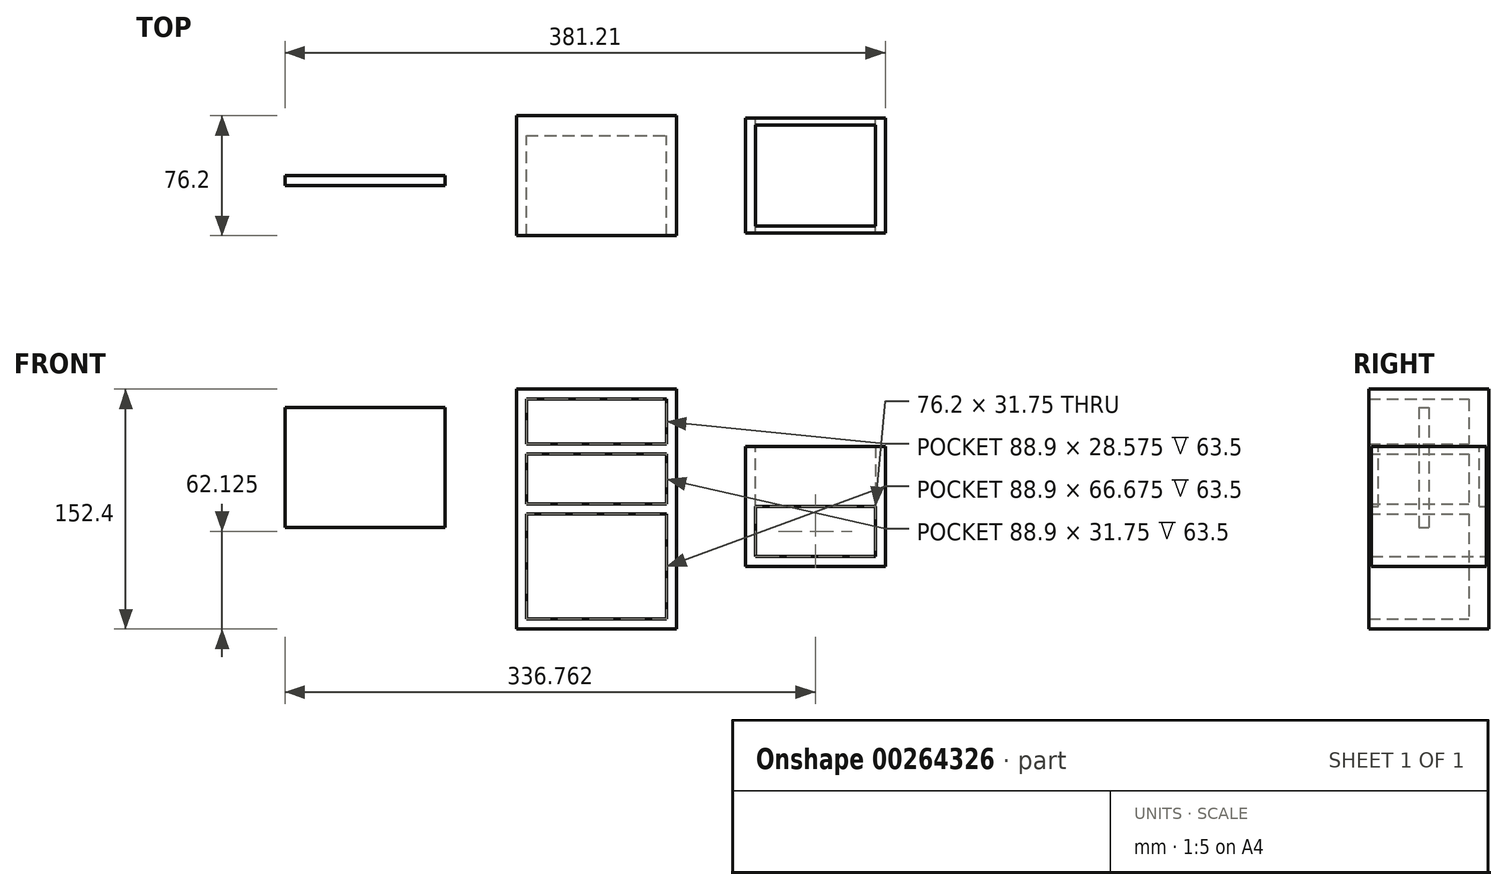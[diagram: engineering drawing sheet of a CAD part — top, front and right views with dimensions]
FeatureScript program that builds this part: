
annotation { "Feature Type Name" : "Feature", "Feature Type Description" : "" }
export const myFeature = defineFeature(function(context is Context, id is Id, definition is map)
    precondition{}
    {
        {
            var Q0;
            Q0=qCreatedBy(makeId("Top.planeOp"),FACE);
            var sketch = newSketch(context, id + "F0", { "sketchPlane" : qUnion([Q0])});
            skLineSegment(sketch, "E0.bottom", {"start": v(-50.8, 38.1) * mm, "end": v(50.8, 38.1) * mm});
            skLineSegment(sketch, "E0.top", {"start": v(-50.8, -38.1) * mm, "end": v(50.8, -38.1) * mm});
            skLineSegment(sketch, "E0.left", {"start": v(-50.8, 38.1) * mm, "end": v(-50.8, -38.1) * mm});
            skLineSegment(sketch, "E0.right", {"start": v(50.8, 38.1) * mm, "end": v(50.8, -38.1) * mm});
            skPoint(sketch, "E0.middle", {"position": v(0, 0) * mm});
            skSolve(sketch);
        }
        {
            var Q0;
            Q0=makeQuery(id+"F0.imprint","IMPRINT",FACE,{"disambiguationData":[TD([[makeQuery(id+"F0.imprint","IMPRINT",EDGE,{"derivedFrom":sQuery(id+"F0.wireOp",EDGE,"E0.bottom")}),-1.0]])]});
            extrude(context, id + "F1", {"entities" : qUnion([Q0]), "endBound" : BoundingType.SYMMETRIC, "depth" : 152.4 * mm});
        }
        {
            var Q0;
            Q0=qCreatedBy(makeId("Front.planeOp"),FACE);
            var sketch = newSketch(context, id + "F2", { "sketchPlane" : qUnion([Q0])});
            skLineSegment(sketch, "E1", {"start": v(0, 0) * mm, "end": v(0, 38.1) * mm});
            skLineSegment(sketch, "E2", {"start": v(0, 0) * mm, "end": v(0, 19.05) * mm});
            skLineSegment(sketch, "E3.bottom", {"start": v(-44.45, 69.85) * mm, "end": v(44.45, 69.85) * mm});
            skLineSegment(sketch, "E3.top", {"start": v(-44.45, -31.75) * mm, "end": v(44.45, -31.75) * mm});
            skLineSegment(sketch, "E3.left", {"start": v(-44.45, 69.85) * mm, "end": v(-44.45, -31.75) * mm});
            skLineSegment(sketch, "E3.right", {"start": v(44.45, 69.85) * mm, "end": v(44.45, -31.75) * mm});
            skPoint(sketch, "E3.middle", {"position": v(0, 19.05) * mm});
            skLineSegment(sketch, "E4", {"start": v(0, -31.75) * mm, "end": v(0, -57.15) * mm});
            skPoint(sketch, "E4.endSnap0", {"position": v(0, -31.75) * mm});
            skLineSegment(sketch, "E5.bottom", {"start": v(-44.45, -44.45) * mm, "end": v(44.45, -44.45) * mm});
            skLineSegment(sketch, "E5.top", {"start": v(-44.45, -69.85) * mm, "end": v(44.45, -69.85) * mm});
            skLineSegment(sketch, "E5.left", {"start": v(-44.45, -44.45) * mm, "end": v(-44.45, -69.85) * mm});
            skLineSegment(sketch, "E5.right", {"start": v(44.45, -44.45) * mm, "end": v(44.45, -69.85) * mm});
            skPoint(sketch, "E5.middle", {"position": v(0, -57.15) * mm});
            skLineSegment(sketch, "E6.bottom", {"start": v(-44.45, 41.28) * mm, "end": v(44.45, 41.28) * mm});
            skLineSegment(sketch, "E6.top", {"start": v(-44.45, 34.92) * mm, "end": v(44.45, 34.92) * mm});
            skLineSegment(sketch, "E6.left", {"start": v(-44.45, 41.28) * mm, "end": v(-44.45, 34.92) * mm});
            skLineSegment(sketch, "E6.right", {"start": v(44.45, 41.28) * mm, "end": v(44.45, 34.92) * mm});
            skPoint(sketch, "E6.middle", {"position": v(0, 38.1) * mm});
            skLineSegment(sketch, "E7.bottom", {"start": v(-44.45, 3.18) * mm, "end": v(44.45, 3.18) * mm});
            skLineSegment(sketch, "E7.top", {"start": v(-44.45, -3.17) * mm, "end": v(44.45, -3.17) * mm});
            skLineSegment(sketch, "E7.left", {"start": v(-44.45, 3.18) * mm, "end": v(-44.45, -3.17) * mm});
            skLineSegment(sketch, "E7.right", {"start": v(44.45, 3.18) * mm, "end": v(44.45, -3.17) * mm});
            skPoint(sketch, "E7.middle", {"position": v(0, 0) * mm});
            skLineSegment(sketch, "E8", {"start": v(-44.45, -44.45) * mm, "end": v(-44.45, -38.1) * mm});
            skLineSegment(sketch, "E9", {"start": v(-44.45, -38.1) * mm, "end": v(44.45, -38.1) * mm});
            skLineSegment(sketch, "E10", {"start": v(44.45, -38.1) * mm, "end": v(44.45, -44.45) * mm});
            skLineSegment(sketch, "E11.bottom", {"start": v(-197.75, 64.7) * mm, "end": v(-96.15, 64.7) * mm});
            skLineSegment(sketch, "E11.top", {"start": v(-197.75, -11.5) * mm, "end": v(-96.15, -11.5) * mm});
            skLineSegment(sketch, "E11.left", {"start": v(-197.75, 64.7) * mm, "end": v(-197.75, -11.5) * mm});
            skLineSegment(sketch, "E11.right", {"start": v(-96.15, 64.7) * mm, "end": v(-96.15, -11.5) * mm});
            skPoint(sketch, "E11.middle", {"position": v(-146.95, 26.6) * mm});
            skLineSegment(sketch, "E12", {"start": v(-44.45, -31.75) * mm, "end": v(-44.45, -38.1) * mm});
            skLineSegment(sketch, "E13", {"start": v(44.45, -31.75) * mm, "end": v(44.45, -38.1) * mm});
            skPoint(sketch, "E14.middle", {"position": v(139.01, 1.8) * mm});
            skLineSegment(sketch, "E15.bottom", {"start": v(94.56, -36.3) * mm, "end": v(183.46, -36.3) * mm});
            skLineSegment(sketch, "E15.left", {"start": v(94.56, -36.3) * mm, "end": v(94.56, 39.9) * mm});
            skLineSegment(sketch, "E15.right", {"start": v(183.46, -36.3) * mm, "end": v(183.46, 39.9) * mm});
            skLineSegment(sketch, "E16", {"start": v(94.56, -29.95) * mm, "end": v(183.46, -29.95) * mm});
            skLineSegment(sketch, "E17", {"start": v(139.01, 1.8) * mm, "end": v(139.01, 39.9) * mm});
            skLineSegment(sketch, "E18", {"start": v(139.01, 39.9) * mm, "end": v(94.56, 39.9) * mm});
            skLineSegment(sketch, "E19", {"start": v(139.01, 39.9) * mm, "end": v(183.46, 39.9) * mm});
            skLineSegment(sketch, "E20", {"start": v(139.01, 1.8) * mm, "end": v(100.91, 1.8) * mm});
            skLineSegment(sketch, "E21", {"start": v(100.91, 1.8) * mm, "end": v(139.01, 1.8) * mm});
            skLineSegment(sketch, "E22", {"start": v(177.11, 1.8) * mm, "end": v(139.01, 1.8) * mm});
            skLineSegment(sketch, "E23", {"start": v(100.91, 1.8) * mm, "end": v(100.91, -36.3) * mm});
            skLineSegment(sketch, "E24", {"start": v(100.91, -36.3) * mm, "end": v(100.91, 39.9) * mm});
            skLineSegment(sketch, "E25", {"start": v(100.91, 39.9) * mm, "end": v(177.11, 39.9) * mm});
            skLineSegment(sketch, "E26", {"start": v(177.11, 39.9) * mm, "end": v(177.11, 1.8) * mm});
            skLineSegment(sketch, "E27", {"start": v(177.11, -29.95) * mm, "end": v(177.11, 1.8) * mm});
            skLineSegment(sketch, "E28", {"start": v(139.01, 39.9) * mm, "end": v(139.01, 33.55) * mm});
            skLineSegment(sketch, "E29", {"start": v(139.01, 33.55) * mm, "end": v(183.46, 33.55) * mm});
            skLineSegment(sketch, "E30", {"start": v(183.46, 33.55) * mm, "end": v(94.56, 33.55) * mm});
            skSolve(sketch);
        }
        {
            var Q0;
            Q0=makeQuery(id+"F2.imprint","IMPRINT",FACE,{"disambiguationData":[TD([[makeQuery(id+"F2.imprint","IMPRINT",EDGE,{"derivedFrom":sQuery(id+"F2.wireOp",EDGE,"E3.bottom")}),-1.0]])]});
            var Q1;
            Q1=makeQuery(id+"F2.imprint","IMPRINT",FACE,{"disambiguationData":[TD([[makeQuery(id+"F2.imprint","IMPRINT",EDGE,{"derivedFrom":sQuery(id+"F2.wireOp",EDGE,"E5.top")}),1.0]])]});
            var Q2;
            {var subQ5=sQuery(id+"F2.wireOp",EDGE,"E2");var subQ6=sQuery(id+"F2.wireOp",EDGE,"E1");var subQ7=makeQuery(id+"F2.imprint","INTERSECT",VERTEX,{"derivedFrom":[subQ6,subQ5]});Q2=makeQuery(id+"F2.imprint","IMPRINT",FACE,{"disambiguationData":[TD([[makeQuery(id+"F2.imprint","IMPRINT",EDGE,{"disambiguationData":[TD([[subQ7,-1.0]])],"derivedFrom":subQ6}),1.0]])]});}
            var Q3;
            {var subQ5=sQuery(id+"F2.wireOp",EDGE,"E2");var subQ7=sQuery(id+"F2.wireOp",EDGE,"E1");var subQ9=makeQuery(id+"F2.imprint","INTERSECT",VERTEX,{"derivedFrom":[subQ7,subQ5]});Q3=makeQuery(id+"F2.imprint","IMPRINT",FACE,{"disambiguationData":[TD([[makeQuery(id+"F2.imprint","IMPRINT",EDGE,{"disambiguationData":[TD([[subQ9,-1.0]])],"derivedFrom":subQ7}),-1.0]])]});}
            var Q4;
            {var subQ3=sQuery(id+"F2.wireOp",EDGE,"E7.top");Q4=makeQuery(id+"F2.imprint","IMPRINT",FACE,{"disambiguationData":[TD([[makeQuery(id+"F2.imprint","IMPRINT",EDGE,{"derivedFrom":subQ3}),-1.0]])]});}
            var Q5;
            {var subQ5=sQuery(id+"F2.wireOp",EDGE,"E10");Q5=makeQuery(id+"F2.imprint","IMPRINT",FACE,{"disambiguationData":[TD([[makeQuery(id+"F2.imprint","IMPRINT",EDGE,{"derivedFrom":subQ5}),-1.0]])]});}
            var Q6;
            {var subQ5=sQuery(id+"F2.wireOp",EDGE,"E8");Q6=makeQuery(id+"F2.imprint","IMPRINT",FACE,{"disambiguationData":[TD([[makeQuery(id+"F2.imprint","IMPRINT",EDGE,{"derivedFrom":subQ5}),-1.0]])]});}
            var Q7;
            {var subQ0=sQuery(id+"F2.wireOp",EDGE,"E12");Q7=makeQuery(id+"F2.imprint","IMPRINT",FACE,{"disambiguationData":[TD([[makeQuery(id+"F2.imprint","IMPRINT",EDGE,{"derivedFrom":subQ0}),1.0]])]});}
            var Q8;
            {var subQ0=sQuery(id+"F2.wireOp",EDGE,"E13");Q8=makeQuery(id+"F2.imprint","IMPRINT",FACE,{"disambiguationData":[TD([[makeQuery(id+"F2.imprint","IMPRINT",EDGE,{"derivedFrom":subQ0}),-1.0]])]});}
            extrude(context, id + "F3", {"entities" : qUnion([Q0, Q1, Q2, Q3, Q4, Q5, Q6, Q7, Q8]), "operationType" : NewBodyOperationType.REMOVE, "depth" : 50.8 * mm});
        }
        {
            var Q0;
            Q0=makeQuery(id+"F3.boolean.opBoolean","COPY",FACE,{"derivedFrom":makeQuery(id+"F3.opExtrude","CAP_FACE",FACE,{"disambiguationData":[OSD([sQuery(id+"F2.wireOp",EDGE,"E3.bottom"),sQuery(id+"F2.wireOp",EDGE,"E3.top"),sQuery(id+"F2.wireOp",EDGE,"E3.left"),sQuery(id+"F2.wireOp",EDGE,"E3.right")])],"isStart":true})});
            var Q1;
            Q1=makeQuery(id+"F3.boolean.opBoolean","COPY",FACE,{"derivedFrom":makeQuery(id+"F3.opExtrude","CAP_FACE",FACE,{"disambiguationData":[OSD([sQuery(id+"F2.wireOp",EDGE,"E3.left"),sQuery(id+"F2.wireOp",EDGE,"E3.right"),sQuery(id+"F2.wireOp",EDGE,"E6.top"),sQuery(id+"F2.wireOp",EDGE,"E7.bottom")])],"isStart":true})});
            var Q2;
            Q2=makeQuery(id+"F3.boolean.opBoolean","COPY",FACE,{"derivedFrom":makeQuery(id+"F3.opExtrude","CAP_FACE",FACE,{"disambiguationData":[OSD([sQuery(id+"F2.wireOp",EDGE,"E3.left"),sQuery(id+"F2.wireOp",EDGE,"E3.right"),sQuery(id+"F2.wireOp",EDGE,"E5.top"),sQuery(id+"F2.wireOp",EDGE,"E5.left"),sQuery(id+"F2.wireOp",EDGE,"E5.right"),sQuery(id+"F2.wireOp",EDGE,"E7.top"),sQuery(id+"F2.wireOp",EDGE,"E8"),sQuery(id+"F2.wireOp",EDGE,"E10"),sQuery(id+"F2.wireOp",EDGE,"E12"),sQuery(id+"F2.wireOp",EDGE,"E13")])],"isStart":true})});
            extrude(context, id + "F4", {"entities" : qUnion([Q0, Q1, Q2]), "operationType" : NewBodyOperationType.REMOVE, "oppositeDirection" : true, "depth" : 25.4 * mm});
        }
        {
            var Q0;
            Q0=makeQuery(id+"F2.imprint","IMPRINT",FACE,{"disambiguationData":[TD([[makeQuery(id+"F2.imprint","IMPRINT",EDGE,{"derivedFrom":sQuery(id+"F2.wireOp",EDGE,"E11.bottom")}),-1.0]])]});
            extrude(context, id + "F5", {"entities" : qUnion([Q0]), "depth" : 6.35 * mm});
        }
        {
            var Q0;
            {var subQ2=sQuery(id+"F2.wireOp",EDGE,"E16");var subQ4=sQuery(id+"F2.wireOp",EDGE,"E15.left");var subQ5=makeQuery(id+"F2.imprint","INTERSECT",VERTEX,{"derivedFrom":[subQ4,subQ2]});Q0=makeQuery(id+"F2.imprint","IMPRINT",FACE,{"disambiguationData":[TD([[makeQuery(id+"F2.imprint","IMPRINT",EDGE,{"disambiguationData":[TD([[subQ5,-1.0]])],"derivedFrom":subQ4}),-1.0]])]});}
            var Q1;
            {var subQ0=sQuery(id+"F2.wireOp",EDGE,"E17");Q1=makeQuery(id+"F2.imprint","IMPRINT",FACE,{"disambiguationData":[TD([[makeQuery(id+"F2.imprint","IMPRINT",EDGE,{"derivedFrom":subQ0}),1.0]])]});}
            var Q2;
            {var subQ0=sQuery(id+"F2.wireOp",EDGE,"E17");Q2=makeQuery(id+"F2.imprint","IMPRINT",FACE,{"disambiguationData":[TD([[makeQuery(id+"F2.imprint","IMPRINT",EDGE,{"derivedFrom":subQ0}),-1.0]])]});}
            var Q3;
            {var subQ1=sQuery(id+"F2.wireOp",EDGE,"E21");Q3=makeQuery(id+"F2.imprint","IMPRINT",FACE,{"disambiguationData":[TD([[makeQuery(id+"F2.imprint","IMPRINT",EDGE,{"derivedFrom":subQ1}),-1.0]])]});}
            var Q4;
            {var subQ0=sQuery(id+"F2.wireOp",EDGE,"E27");Q4=makeQuery(id+"F2.imprint","IMPRINT",FACE,{"disambiguationData":[TD([[makeQuery(id+"F2.imprint","IMPRINT",EDGE,{"derivedFrom":subQ0}),-1.0]])]});}
            var Q5;
            {var subQ0=sQuery(id+"F2.wireOp",EDGE,"E19");Q5=makeQuery(id+"F2.imprint","IMPRINT",FACE,{"disambiguationData":[TD([[makeQuery(id+"F2.imprint","IMPRINT",EDGE,{"derivedFrom":subQ0}),-1.0]])]});}
            var Q6;
            {var subQ3=sQuery(id+"F2.wireOp",EDGE,"E28");Q6=makeQuery(id+"F2.imprint","IMPRINT",FACE,{"disambiguationData":[TD([[makeQuery(id+"F2.imprint","IMPRINT",EDGE,{"derivedFrom":subQ3}),1.0]])]});}
            var Q7;
            {var subQ5=sQuery(id+"F2.wireOp",EDGE,"E28");Q7=makeQuery(id+"F2.imprint","IMPRINT",FACE,{"disambiguationData":[TD([[makeQuery(id+"F2.imprint","IMPRINT",EDGE,{"derivedFrom":subQ5}),-1.0]])]});}
            var Q8;
            {var subQ0=sQuery(id+"F2.wireOp",EDGE,"E18");Q8=makeQuery(id+"F2.imprint","IMPRINT",FACE,{"disambiguationData":[TD([[makeQuery(id+"F2.imprint","IMPRINT",EDGE,{"derivedFrom":subQ0}),1.0]])]});}
            var Q9;
            {var subQ0=sQuery(id+"F2.wireOp",EDGE,"E15.left");var subQ1=sQuery(id+"F2.wireOp",EDGE,"E15.bottom");var subQ2=makeQuery(id+"F2.imprint","INTERSECT",VERTEX,{"derivedFrom":[subQ1,subQ0]});Q9=makeQuery(id+"F2.imprint","IMPRINT",FACE,{"disambiguationData":[TD([[makeQuery(id+"F2.imprint","IMPRINT",EDGE,{"disambiguationData":[TD([[subQ2,-1.0]])],"derivedFrom":subQ1}),1.0]])]});}
            var Q10;
            {var subQ1=sQuery(id+"F2.wireOp",EDGE,"E15.right");var subQ4=sQuery(id+"F2.wireOp",EDGE,"E15.bottom");var subQ5=makeQuery(id+"F2.imprint","INTERSECT",VERTEX,{"derivedFrom":[subQ4,subQ1]});Q10=makeQuery(id+"F2.imprint","IMPRINT",FACE,{"disambiguationData":[TD([[makeQuery(id+"F2.imprint","IMPRINT",EDGE,{"disambiguationData":[TD([[subQ5,1.0]])],"derivedFrom":subQ4}),1.0]])]});}
            extrude(context, id + "F6", {"entities" : qUnion([Q0, Q1, Q2, Q3, Q4, Q5, Q6, Q7, Q8, Q9, Q10]), "endBound" : BoundingType.SYMMETRIC, "depth" : 73.02 * mm});
        }
        {
            var Q0;
            {var subQ5=sQuery(id+"F2.wireOp",EDGE,"E28");Q0=makeQuery(id+"F2.imprint","IMPRINT",FACE,{"disambiguationData":[TD([[makeQuery(id+"F2.imprint","IMPRINT",EDGE,{"derivedFrom":subQ5}),-1.0]])]});}
            var Q1;
            {var subQ3=sQuery(id+"F2.wireOp",EDGE,"E28");Q1=makeQuery(id+"F2.imprint","IMPRINT",FACE,{"disambiguationData":[TD([[makeQuery(id+"F2.imprint","IMPRINT",EDGE,{"derivedFrom":subQ3}),1.0]])]});}
            var Q2;
            {var subQ0=sQuery(id+"F2.wireOp",EDGE,"E17");Q2=makeQuery(id+"F2.imprint","IMPRINT",FACE,{"disambiguationData":[TD([[makeQuery(id+"F2.imprint","IMPRINT",EDGE,{"derivedFrom":subQ0}),-1.0]])]});}
            var Q3;
            {var subQ0=sQuery(id+"F2.wireOp",EDGE,"E17");Q3=makeQuery(id+"F2.imprint","IMPRINT",FACE,{"disambiguationData":[TD([[makeQuery(id+"F2.imprint","IMPRINT",EDGE,{"derivedFrom":subQ0}),1.0]])]});}
            var Q4;
            {var subQ1=sQuery(id+"F2.wireOp",EDGE,"E21");Q4=makeQuery(id+"F2.imprint","IMPRINT",FACE,{"disambiguationData":[TD([[makeQuery(id+"F2.imprint","IMPRINT",EDGE,{"derivedFrom":subQ1}),-1.0]])]});}
            extrude(context, id + "F7", {"entities" : qUnion([Q0, Q1, Q2, Q3, Q4]), "operationType" : NewBodyOperationType.REMOVE, "endBound" : BoundingType.SYMMETRIC, "depth" : 64.13 * mm});
        }
    });
